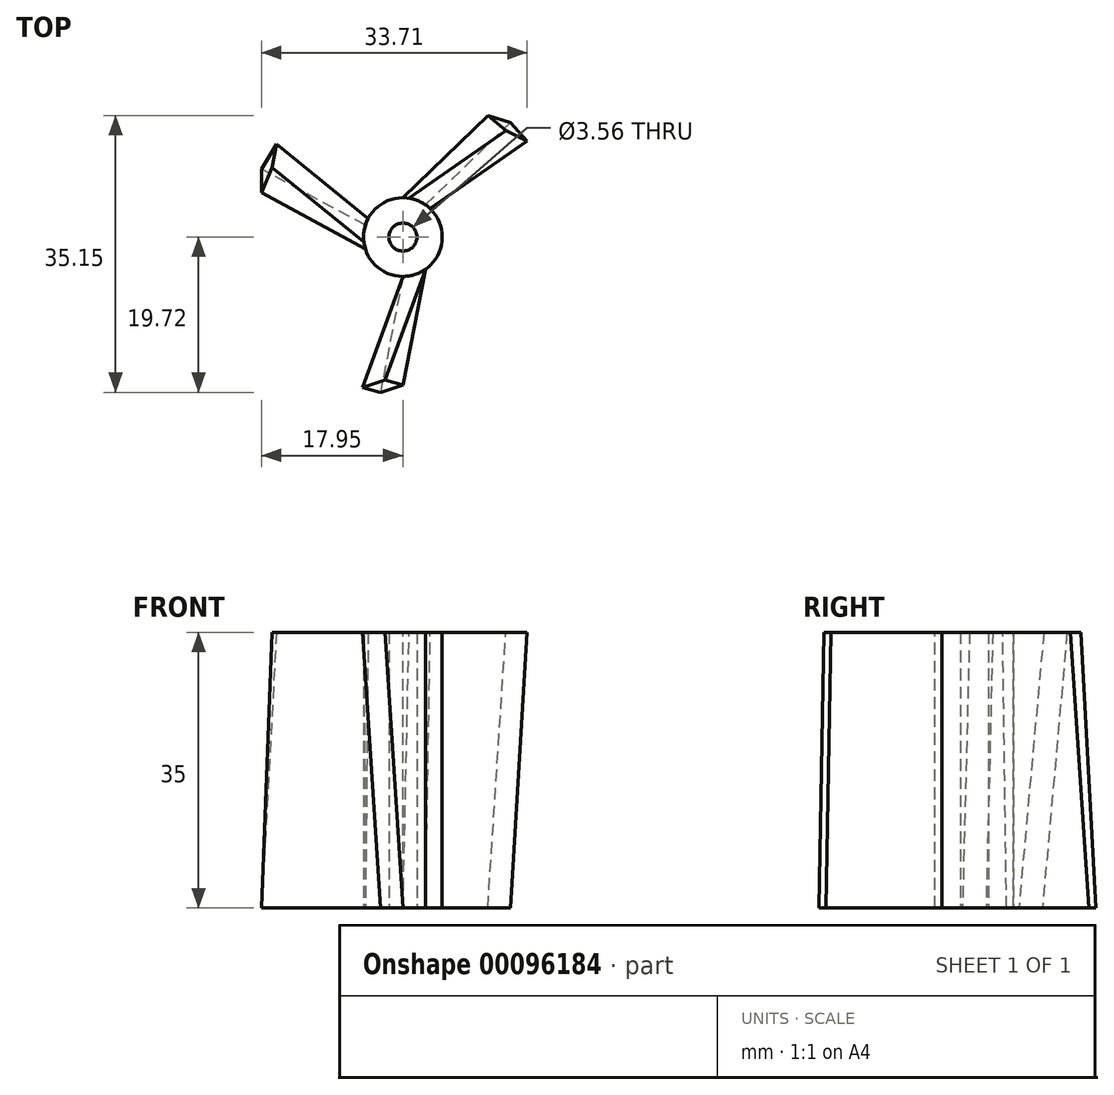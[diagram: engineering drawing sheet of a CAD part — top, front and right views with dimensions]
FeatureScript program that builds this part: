
annotation { "Feature Type Name" : "Feature", "Feature Type Description" : "" }
export const myFeature = defineFeature(function(context is Context, id is Id, definition is map)
    precondition{}
    {
        {
            var Q0;
            Q0=qCreatedBy(makeId("Top.planeOp"),FACE);
            var sketch = newSketch(context, id + "F0", { "sketchPlane" : qUnion([Q0])});
            skCircle(sketch, "E0", {"center": v(0, 0) * mm, "radius": 5 * mm});
            skCircle(sketch, "E1", {"center": v(0, 0) * mm, "radius": 1.78 * mm});
            skPoint(sketch, "E2", {"position": v(0, 5) * mm});
            skPoint(sketch, "E3", {"position": v(0, -5) * mm});
            skPoint(sketch, "E4", {"position": v(2.86, 4.1) * mm});
            skLineSegment(sketch, "E5", {"start": v(0, 5) * mm, "end": v(2.86, 4.1) * mm, "construction": true});
            skPoint(sketch, "E6", {"position": v(2.86, -4.1) * mm});
            skLineSegment(sketch, "E7", {"start": v(0, -5) * mm, "end": v(2.86, -4.1) * mm, "construction": true});
            skLineSegment(sketch, "E8", {"start": v(-4.77, 1.5) * mm, "end": v(-4.77, -1.5) * mm, "construction": true});
            skPoint(sketch, "E9", {"position": v(-4.77, 0) * mm});
            skLineSegment(sketch, "E10", {"start": v(0, 5) * mm, "end": v(10.78, 15.43) * mm});
            skLineSegment(sketch, "E11", {"start": v(2.86, 4.1) * mm, "end": v(13.64, 14.53) * mm});
            skLineSegment(sketch, "E12", {"start": v(10.78, 15.43) * mm, "end": v(13.64, 14.53) * mm});
            skLineSegment(sketch, "E13", {"start": v(-4.77, -1.5) * mm, "end": v(-17.95, 5.66) * mm});
            skLineSegment(sketch, "E14", {"start": v(-4.77, 1.5) * mm, "end": v(-17.95, 8.66) * mm});
            skLineSegment(sketch, "E15", {"start": v(-17.95, 5.66) * mm, "end": v(-17.95, 8.66) * mm});
            skLineSegment(sketch, "E16", {"start": v(2.86, -4.1) * mm, "end": v(0, -18.82) * mm});
            skLineSegment(sketch, "E17", {"start": v(0, -5) * mm, "end": v(-2.86, -19.72) * mm});
            skLineSegment(sketch, "E18", {"start": v(0, -18.82) * mm, "end": v(-2.86, -19.72) * mm});
            skSolve(sketch);
        }
        {
            var Q0;
            Q0=qCreatedBy(makeId("Top.planeOp"),FACE);
            cPlane(context, id + "F1", {"entities" : qUnion([Q0]), "cplaneType" : CPlaneType.OFFSET, "offset" : 35 * mm, "width" : 150 * mm, "height" : 150 * mm});
        }
        {
            var Q0;
            Q0=qCreatedBy(id+"F1.planeOp",FACE);
            var sketch = newSketch(context, id + "F2", { "sketchPlane" : qUnion([Q0])});
            skCircle(sketch, "E19", {"center": v(0, 0) * mm, "radius": 5 * mm});
            skCircle(sketch, "E20", {"center": v(0, 0) * mm, "radius": 1.78 * mm});
            skPoint(sketch, "E21", {"position": v(0.79, 4.94) * mm});
            skPoint(sketch, "E22", {"position": v(0, -5) * mm});
            skPoint(sketch, "E23", {"position": v(3.47, 3.6) * mm});
            skLineSegment(sketch, "E24", {"start": v(0.79, 4.94) * mm, "end": v(3.47, 3.6) * mm});
            skPoint(sketch, "E25", {"position": v(2.86, -4.1) * mm});
            skLineSegment(sketch, "E26", {"start": v(0, -5) * mm, "end": v(2.86, -4.1) * mm});
            skLineSegment(sketch, "E27", {"start": v(0.79, 4.94) * mm, "end": v(13.07, 13.54) * mm});
            skLineSegment(sketch, "E28", {"start": v(3.47, 3.6) * mm, "end": v(15.76, 12.2) * mm});
            skLineSegment(sketch, "E29", {"start": v(13.07, 13.54) * mm, "end": v(15.76, 12.2) * mm});
            skLineSegment(sketch, "E30", {"start": v(-4.96, -0.6) * mm, "end": v(-16.62, 8.83) * mm});
            skLineSegment(sketch, "E31", {"start": v(-4.42, 2.34) * mm, "end": v(-16.07, 11.78) * mm});
            skLineSegment(sketch, "E32", {"start": v(-16.62, 8.83) * mm, "end": v(-16.07, 11.78) * mm});
            skLineSegment(sketch, "E33", {"start": v(2.86, -4.1) * mm, "end": v(-2.29, -18.19) * mm});
            skLineSegment(sketch, "E34", {"start": v(0, -5) * mm, "end": v(-5.15, -19.09) * mm});
            skLineSegment(sketch, "E35", {"start": v(-2.29, -18.19) * mm, "end": v(-5.15, -19.09) * mm});
            skLineSegment(sketch, "E36", {"start": v(-5.15, -19.09) * mm, "end": v(0, -19.09) * mm, "construction": true});
            skLineSegment(sketch, "E37", {"start": v(-16.62, 8.83) * mm, "end": v(-16.62, 0) * mm, "construction": true});
            skSolve(sketch);
        }
        {
            var Q0;
            {var subQ3=sQuery(id+"F0.wireOp",EDGE,"E16");Q0=makeQuery(id+"F0.imprint","IMPRINT",FACE,{"disambiguationData":[TD([[makeQuery(id+"F0.imprint","IMPRINT",EDGE,{"derivedFrom":subQ3}),-1.0]])]});}
            var Q1;
            {var subQ3=sQuery(id+"F2.wireOp",EDGE,"E33");Q1=makeQuery(id+"F2.imprint","IMPRINT",FACE,{"disambiguationData":[TD([[makeQuery(id+"F2.imprint","IMPRINT",EDGE,{"derivedFrom":subQ3}),-1.0]])]});}
            loft(context, id + "F3", {"sheetProfilesArray" : [{ "sheetProfileEntities" : qUnion([Q0]) }, { "sheetProfileEntities" : qUnion([Q1]) }]});
        }
        {
            var Q0;
            {var subQ0=sQuery(id+"F0.wireOp",EDGE,"E10");Q0=makeQuery(id+"F0.imprint","IMPRINT",FACE,{"disambiguationData":[TD([[makeQuery(id+"F0.imprint","IMPRINT",EDGE,{"derivedFrom":subQ0}),-1.0]])]});}
            var Q1;
            {var subQ0=sQuery(id+"F2.wireOp",EDGE,"E27");Q1=makeQuery(id+"F2.imprint","IMPRINT",FACE,{"disambiguationData":[TD([[makeQuery(id+"F2.imprint","IMPRINT",EDGE,{"derivedFrom":subQ0}),-1.0]])]});}
            loft(context, id + "F4", {"sheetProfilesArray" : [{ "sheetProfileEntities" : qUnion([Q0]) }, { "sheetProfileEntities" : qUnion([Q1]) }]});
        }
        {
            var Q0;
            {var subQ0=sQuery(id+"F2.wireOp",EDGE,"E30");Q0=makeQuery(id+"F2.imprint","IMPRINT",FACE,{"disambiguationData":[TD([[makeQuery(id+"F2.imprint","IMPRINT",EDGE,{"derivedFrom":subQ0}),-1.0]])]});}
            var Q1;
            {var subQ0=sQuery(id+"F0.wireOp",EDGE,"E13");Q1=makeQuery(id+"F0.imprint","IMPRINT",FACE,{"disambiguationData":[TD([[makeQuery(id+"F0.imprint","IMPRINT",EDGE,{"derivedFrom":subQ0}),-1.0]])]});}
            loft(context, id + "F5", {"sheetProfilesArray" : [{ "sheetProfileEntities" : qUnion([Q0]) }, { "sheetProfileEntities" : qUnion([Q1]) }]});
        }
        {
            var Q0;
            Q0=makeQuery(id+"F0.imprint","IMPRINT",FACE,{"disambiguationData":[TD([[makeQuery(id+"F0.imprint","IMPRINT",EDGE,{"derivedFrom":sQuery(id+"F0.wireOp",EDGE,"E1")}),-1.0]])]});
            extrude(context, id + "F6", {"entities" : qUnion([Q0]), "depth" : 35 * mm});
        }
    });
